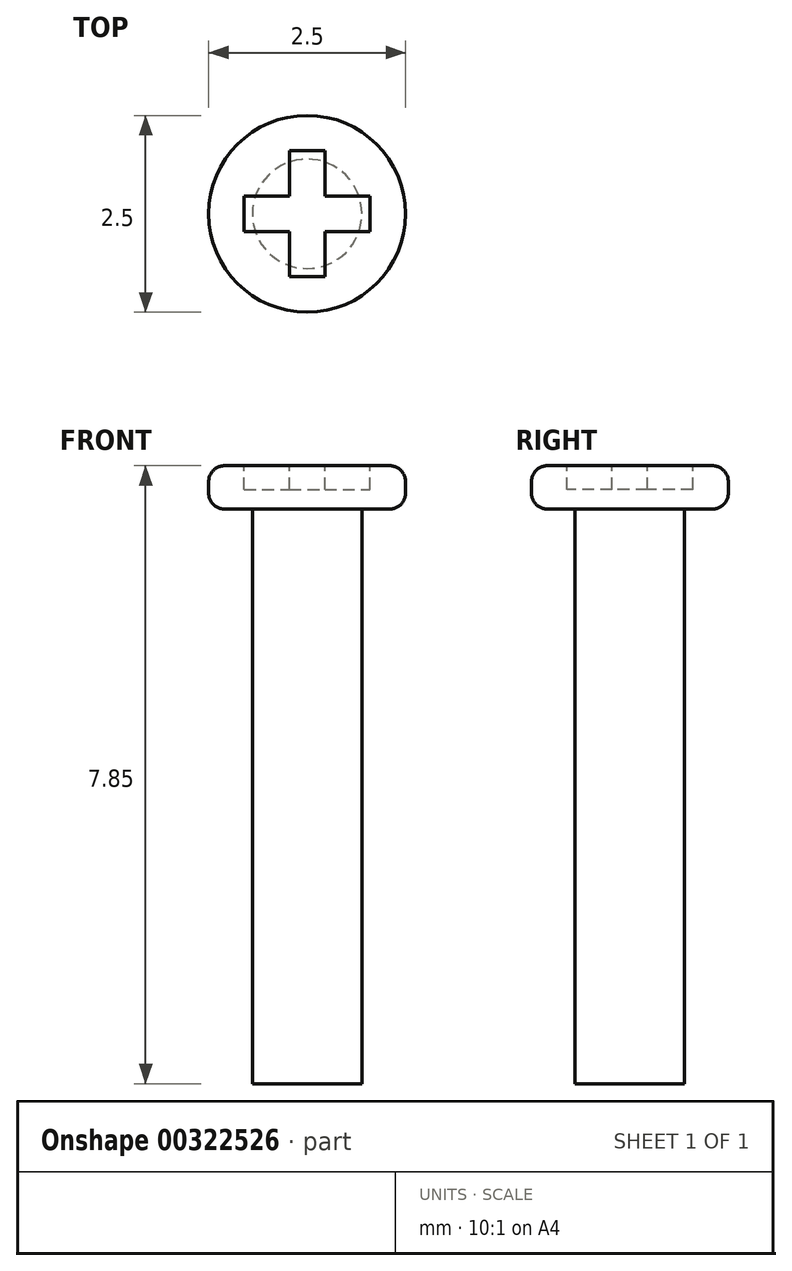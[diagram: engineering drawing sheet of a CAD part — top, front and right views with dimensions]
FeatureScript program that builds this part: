
annotation { "Feature Type Name" : "Feature", "Feature Type Description" : "" }
export const myFeature = defineFeature(function(context is Context, id is Id, definition is map)
    precondition{}
    {
        {
            var Q0;
            Q0=qCreatedBy(makeId("Top.planeOp"),FACE);
            var sketch = newSketch(context, id + "F0", { "sketchPlane" : qUnion([Q0])});
            skCircle(sketch, "E0", {"center": v(0, 0) * mm, "radius": 1.25 * mm});
            skSolve(sketch);
        }
        {
            var Q0;
            Q0=makeQuery(id+"F0.imprint","IMPRINT",FACE,{"disambiguationData":[TD([[makeQuery(id+"F0.imprint","IMPRINT",EDGE,{"derivedFrom":sQuery(id+"F0.wireOp",EDGE,"E0")}),1.0]])]});
            extrude(context, id + "F1", {"entities" : qUnion([Q0]), "depth" : .55 * mm});
        }
        {
            var Q0;
            Q0=makeQuery(id+"F1.opExtrude","CAP_FACE",FACE,{"disambiguationData":[OSD([sQuery(id+"F0.wireOp",EDGE,"E0")])],"isStart":true});
            var sketch = newSketch(context, id + "F2", { "sketchPlane" : qUnion([Q0])});
            skCircle(sketch, "E1", {"center": v(0, 0) * mm, "radius": 0.7 * mm});
            skSolve(sketch);
        }
        {
            var Q0;
            Q0=makeQuery(id+"F2.imprint","IMPRINT",FACE,{"disambiguationData":[TD([[makeQuery(id+"F2.imprint","IMPRINT",EDGE,{"derivedFrom":sQuery(id+"F2.wireOp",EDGE,"E1")}),1.0]])]});
            extrude(context, id + "F3", {"entities" : qUnion([Q0]), "operationType" : NewBodyOperationType.ADD, "depth" : 7.3 * mm});
        }
        {
            var Q0;
            Q0=makeQuery(id+"F1.opExtrude","CAP_FACE",FACE,{"disambiguationData":[OSD([sQuery(id+"F0.wireOp",EDGE,"E0")])],"isStart":false});
            var sketch = newSketch(context, id + "F4", { "sketchPlane" : qUnion([Q0])});
            skLineSegment(sketch, "E2.bottom", {"start": v(-0.23, 0.8) * mm, "end": v(0.23, 0.8) * mm});
            skLineSegment(sketch, "E2.top", {"start": v(-0.22, -0.8) * mm, "end": v(0.23, -0.8) * mm});
            skLineSegment(sketch, "E2.left", {"start": v(-0.23, 0.8) * mm, "end": v(-0.22, -0.8) * mm});
            skLineSegment(sketch, "E2.right", {"start": v(0.22, 0.8) * mm, "end": v(0.23, -0.8) * mm});
            skLineSegment(sketch, "E3.bottom", {"start": v(-0.8, 0.23) * mm, "end": v(0.8, 0.23) * mm});
            skLineSegment(sketch, "E3.top", {"start": v(-0.8, -0.23) * mm, "end": v(0.8, -0.23) * mm});
            skLineSegment(sketch, "E3.left", {"start": v(-0.8, 0.23) * mm, "end": v(-0.8, -0.23) * mm});
            skLineSegment(sketch, "E3.right", {"start": v(0.8, 0.23) * mm, "end": v(0.8, -0.23) * mm});
            skSolve(sketch);
        }
        {
            var Q0;
            {var subQ0=sQuery(id+"F4.wireOp",EDGE,"E3.bottom");var subQ1=sQuery(id+"F4.wireOp",EDGE,"E2.left");var subQ2=makeQuery(id+"F4.imprint","INTERSECT",VERTEX,{"derivedFrom":[subQ1,subQ0]});Q0=makeQuery(id+"F4.imprint","IMPRINT",FACE,{"disambiguationData":[TD([[makeQuery(id+"F4.imprint","IMPRINT",EDGE,{"disambiguationData":[TD([[subQ2,-1.0]])],"derivedFrom":subQ1}),1.0]])]});}
            var Q1;
            {var subQ0=sQuery(id+"F4.wireOp",EDGE,"E2.bottom");Q1=makeQuery(id+"F4.imprint","IMPRINT",FACE,{"disambiguationData":[TD([[makeQuery(id+"F4.imprint","IMPRINT",EDGE,{"derivedFrom":subQ0}),-1.0]])]});}
            var Q2;
            {var subQ5=sQuery(id+"F4.wireOp",EDGE,"E3.left");Q2=makeQuery(id+"F4.imprint","IMPRINT",FACE,{"disambiguationData":[TD([[makeQuery(id+"F4.imprint","IMPRINT",EDGE,{"derivedFrom":subQ5}),1.0]])]});}
            var Q3;
            {var subQ0=sQuery(id+"F4.wireOp",EDGE,"E2.top");Q3=makeQuery(id+"F4.imprint","IMPRINT",FACE,{"disambiguationData":[TD([[makeQuery(id+"F4.imprint","IMPRINT",EDGE,{"derivedFrom":subQ0}),1.0]])]});}
            var Q4;
            {var subQ5=sQuery(id+"F4.wireOp",EDGE,"E3.right");Q4=makeQuery(id+"F4.imprint","IMPRINT",FACE,{"disambiguationData":[TD([[makeQuery(id+"F4.imprint","IMPRINT",EDGE,{"derivedFrom":subQ5}),-1.0]])]});}
            extrude(context, id + "F5", {"entities" : qUnion([Q0, Q1, Q2, Q3, Q4]), "operationType" : NewBodyOperationType.REMOVE, "oppositeDirection" : true, "depth" : .3 * mm});
        }
        {
            var Q0;
            Q0=makeQuery(id+"F1.opExtrude","CAP_EDGE",EDGE,{"disambiguationData":[OSD([sQuery(id+"F0.wireOp",EDGE,"E0")])],"isStart":false});
            var Q1;
            Q1=makeQuery(id+"F1.opExtrude","CAP_EDGE",EDGE,{"disambiguationData":[OSD([sQuery(id+"F0.wireOp",EDGE,"E0")])],"isStart":true});
            fillet(context, id + "F6", {"entities" : qUnion([Q0, Q1]), "radius" : .2 * mm, "tangentPropagation" : true, "allowEdgeOverflow" : false});
        }
    });
